# Revit family: XXXCheck_Valve-Grohe-Universal-14232_Series
name_source: partatom
category: Pipe Accessories
units: mm (PartAtom-declared; Revit-internal decimal feet)

## family parameters
Always vertical = Yes
Cut with Voids When Loaded = Yes
OmniClass Number = 23.65.55.14.17
OmniClass Title = Adjusting/Controlling Valves for Liquid Services
Part Type = Normal
Round Connector Dimension = Use Diameter
Shared = Yes
Work Plane-Based = Yes

## types (5) — shared parameters
ADA Compliant = Yes
Assembly Code = D2090600
Connection Size = 1/2"
Default Elevation = 0"
Description = UNIVERSAL Check Valve
Diameter = 1/2"
Height = 1 1/16"
Manufacturer = GROHE
URL = https://www.grohe.us

## per-type parameters (varying)
| type | Compliance Certifications | Finish | Material |
| 14232000 | CSA compliant when installed to the specific requirements of these regulations | Metal-Grohe-000-StarLight Chrome | Metal-Grohe-000-StarLight Chrome |
| 142322430 | ADA, CSA compliant when installed to the specific requirements of these regulations | Metal-Grohe-430-Matte Black | Metal-Grohe-430-Matte Black |
| 14232A00 | ADA, CSA compliant when installed to the specific requirements of these regulations | Metal-Grohe-A00-Hard Graphite | Metal-Grohe-A00-Hard Graphite |
| 14232EN0 | ADA, CSA compliant when installed to the specific requirements of these regulations | Metal-Grohe-Brushed Nickel Infinity Finish | Metal-Grohe-Brushed Nickel Infinity Finish |
| 14232GN0 | ADA, CSA compliant when installed to the specific requirements of these regulations | Metal-Grohe-Brushed Cool Sunrise | Metal-Grohe-Brushed Nickel Infinity Finish |

note: column(s) folded — value = type name in every type: Model

## geometry (parser evidence)
native form markers: Sweep x2
no freeform markers — native parametric forms only
